FCSTD DOCUMENT  (FreeCAD 2024.2R38021 (Git))
Label: Profile__2020-V-Slot
License: All rights reserved
LicenseURL: https://en.wikipedia.org/wiki/All_rights_reserved
objects: Sketcher::SketchObject×1, PartDesign::Body×1
note: 2 computed .brp shape members not serialized (recipe doc carries the construction recipe); baked Part::Feature solids carry a one-line shape summary decoded from their .brp

FEATURE [Sketcher::SketchObject] Sketch
  AttachmentSupport = -> [YZ_Plane]
  FullyConstrained = true
  MapMode = 5
  Placement = pos=(0,0,0) rot=(0.57735,0.57735,0.57735;2.0944rad)
  sketch-geometry (61):
    g0: LineSegment StartX=-5.5 StartY=10 StartZ=0 EndX=-3.7 EndY=8.2 EndZ=0
    g1: LineSegment StartX=-3.7 StartY=8.2 StartZ=0 EndX=-5.5 EndY=8.2 EndZ=0
    g2: LineSegment StartX=-5.5 StartY=8.2 StartZ=0 EndX=-5.5 EndY=6.561 EndZ=0
    g3: LineSegment StartX=-5.5 StartY=6.561 StartZ=0 EndX=-2.639 EndY=3.7 EndZ=0
    g4: LineSegment StartX=-2.639 StartY=3.7 StartZ=0 EndX=-0.4 EndY=3.7 EndZ=0
    g5: LineSegment StartX=-10 StartY=5.5 StartZ=0 EndX=-8.2 EndY=3.7 EndZ=0
    g6: LineSegment StartX=-8.2 StartY=5.5 StartZ=0 EndX=-6.561 EndY=5.5 EndZ=0
    g7: LineSegment StartX=-6.561 StartY=5.5 StartZ=0 EndX=-3.7 EndY=2.639 EndZ=0
    g8: LineSegment StartX=-3.7 StartY=2.639 StartZ=0 EndX=-3.7 EndY=0.4 EndZ=0
    g9: LineSegment StartX=-10 StartY=5.5 StartZ=0 EndX=-10 EndY=10 EndZ=0
    g10: LineSegment StartX=-5.5 StartY=10 StartZ=0 EndX=-10 EndY=10 EndZ=0
    g11: LineSegment StartX=-10 StartY=10 StartZ=0 EndX=-1 EndY=1 EndZ=0
    g12: LineSegment StartX=-8.2 StartY=3.7 StartZ=0 EndX=-8.2 EndY=5.5 EndZ=0
    g13: LineSegment StartX=5.5 StartY=10 StartZ=0 EndX=3.7 EndY=8.2 EndZ=0
    g14: LineSegment StartX=3.7 StartY=8.2 StartZ=0 EndX=5.5 EndY=8.2 EndZ=0
    g15: LineSegment StartX=5.5 StartY=8.2 StartZ=0 EndX=5.5 EndY=6.561 EndZ=0
    g16: LineSegment StartX=5.5 StartY=6.561 StartZ=0 EndX=2.639 EndY=3.7 EndZ=0
    g17: LineSegment StartX=2.639 StartY=3.7 StartZ=0 EndX=0.4 EndY=3.7 EndZ=0
    g18: LineSegment StartX=10 StartY=5.5 StartZ=0 EndX=8.2 EndY=3.7 EndZ=0
    g19: LineSegment StartX=8.2 StartY=5.5 StartZ=0 EndX=6.561 EndY=5.5 EndZ=0
    g20: LineSegment StartX=6.561 StartY=5.5 StartZ=0 EndX=3.7 EndY=2.639 EndZ=0
    g21: LineSegment StartX=3.7 StartY=2.639 StartZ=0 EndX=3.7 EndY=0.4 EndZ=0
    g22: LineSegment StartX=10 StartY=5.5 StartZ=0 EndX=10 EndY=10 EndZ=0
    g23: LineSegment StartX=5.5 StartY=10 StartZ=0 EndX=10 EndY=10 EndZ=0
    g24: LineSegment StartX=10 StartY=10 StartZ=0 EndX=1 EndY=1 EndZ=0
    g25: LineSegment StartX=8.2 StartY=3.7 StartZ=0 EndX=8.2 EndY=5.5 EndZ=0
    g26: LineSegment StartX=-5.5 StartY=-10 StartZ=0 EndX=-3.7 EndY=-8.2 EndZ=0
    g27: LineSegment StartX=-3.7 StartY=-8.2 StartZ=0 EndX=-5.5 EndY=-8.2 EndZ=0
    g28: LineSegment StartX=-5.5 StartY=-8.2 StartZ=0 EndX=-5.5 EndY=-6.561 EndZ=0
    g29: LineSegment StartX=-5.5 StartY=-6.561 StartZ=0 EndX=-2.639 EndY=-3.7 EndZ=0
    g30: LineSegment StartX=-2.639 StartY=-3.7 StartZ=0 EndX=-0.4 EndY=-3.7 EndZ=0
    g31: LineSegment StartX=-10 StartY=-5.5 StartZ=0 EndX=-8.2 EndY=-3.7 EndZ=0
    g32: LineSegment StartX=-8.2 StartY=-5.5 StartZ=0 EndX=-6.561 EndY=-5.5 EndZ=0
    g33: LineSegment StartX=-6.561 StartY=-5.5 StartZ=0 EndX=-3.7 EndY=-2.639 EndZ=0
    g34: LineSegment StartX=-3.7 StartY=-2.639 StartZ=0 EndX=-3.7 EndY=-0.4 EndZ=0
    g35: LineSegment StartX=-10 StartY=-5.5 StartZ=0 EndX=-10 EndY=-10 EndZ=0
    g36: LineSegment StartX=-5.5 StartY=-10 StartZ=0 EndX=-10 EndY=-10 EndZ=0
    g37: LineSegment StartX=-10 StartY=-10 StartZ=0 EndX=-1 EndY=-1 EndZ=0
    g38: LineSegment StartX=-8.2 StartY=-3.7 StartZ=0 EndX=-8.2 EndY=-5.5 EndZ=0
    g39: LineSegment StartX=5.5 StartY=-10 StartZ=0 EndX=3.7 EndY=-8.2 EndZ=0
    g40: LineSegment StartX=3.7 StartY=-8.2 StartZ=0 EndX=5.5 EndY=-8.2 EndZ=0
    g41: LineSegment StartX=5.5 StartY=-8.2 StartZ=0 EndX=5.5 EndY=-6.561 EndZ=0
    g42: LineSegment StartX=5.5 StartY=-6.561 StartZ=0 EndX=2.639 EndY=-3.7 EndZ=0
    g43: LineSegment StartX=2.639 StartY=-3.7 StartZ=0 EndX=0.4 EndY=-3.7 EndZ=0
    g44: LineSegment StartX=10 StartY=-5.5 StartZ=0 EndX=8.2 EndY=-3.7 EndZ=0
    g45: LineSegment StartX=8.2 StartY=-5.5 StartZ=0 EndX=6.561 EndY=-5.5 EndZ=0
    g46: LineSegment StartX=6.561 StartY=-5.5 StartZ=0 EndX=3.7 EndY=-2.639 EndZ=0
    g47: LineSegment StartX=3.7 StartY=-2.639 StartZ=0 EndX=3.7 EndY=-0.4 EndZ=0
    g48: LineSegment StartX=10 StartY=-5.5 StartZ=0 EndX=10 EndY=-10 EndZ=0
    g49: LineSegment StartX=5.5 StartY=-10 StartZ=0 EndX=10 EndY=-10 EndZ=0
    g50: LineSegment StartX=10 StartY=-10 StartZ=0 EndX=1 EndY=-1 EndZ=0
    g51: LineSegment StartX=8.2 StartY=-3.7 StartZ=0 EndX=8.2 EndY=-5.5 EndZ=0
    g52: LineSegment StartX=-0.4 StartY=3.7 StartZ=0 EndX=0 EndY=3.3 EndZ=0
    g53: LineSegment StartX=0 StartY=3.3 StartZ=0 EndX=0.4 EndY=3.7 EndZ=0
    g54: LineSegment StartX=-0.4 StartY=-3.7 StartZ=0 EndX=1e-16 EndY=-3.3 EndZ=0
    g55: LineSegment StartX=1e-16 StartY=-3.3 StartZ=0 EndX=0.4 EndY=-3.7 EndZ=0
    g56: LineSegment StartX=-3.7 StartY=0.4 StartZ=0 EndX=-3.3 EndY=0 EndZ=0
    g57: LineSegment StartX=-3.7 StartY=-0.4 StartZ=0 EndX=-3.3 EndY=0 EndZ=0
    g58: LineSegment StartX=3.7 StartY=-0.4 StartZ=0 EndX=3.3 EndY=1e-16 EndZ=0
    g59: LineSegment StartX=3.7 StartY=0.4 StartZ=0 EndX=3.3 EndY=1e-16 EndZ=0
    g60: Circle CenterX=0 CenterY=0 CenterZ=0 NormalX=0 NormalY=0 NormalZ=1 AngleXU=0 Radius=2.1
  constraints (134):
    c: Coincident(g1,g2)
    c: Coincident(g3,g4)
    c: Coincident(g6,g7)
    c: Coincident(g7,g8)
    c: Vertical(g8)
    c: DistanceY(g-1,g5) = 5.5
    c: DistanceX(g5,g5) = 1.8
    c: Distance(g8,g-1) = 0.4
    c: DistanceY(g-1,g9) = 10
    c: DistanceX(g9,g-1) = 10
    c: Coincident(g9,g5)
    c: Vertical(g9)
    c: Coincident(g10,g0)
    c: Angle(g5,g9) = 2.35619
    c: Coincident(g11,g9)
    c: Distance(g6,g-1) = 5.5
    c: Horizontal(g6)
    c: Coincident(g12,g5)
    c: Coincident(g12,g6)
    c: Vertical(g12)
    c: DistanceY(g8,g8) = 2.239
    c: Symmetric(g5,g0,g11)
    c: Symmetric(g6,g1,g11)
    c: Symmetric(g6,g2,g11)
    c: Symmetric(g7,g3,g11)
    c: Symmetric(g8,g4,g11)
    c: Symmetric(g5,g1,g11)
    c: Coincident(g0,g1)
    c: Coincident(g9,g10)
    c: Coincident(g3,g2)
    c: DistanceX(g6,g6) = 1.639
    c: Angle(g11) = -0.785398
    c: Distance(g11,g-2) = 1
    c: DistanceX(g8,g-1) = 3.7
    c: Symmetric(g0,g13,g-2)
    c: Symmetric(g0,g13,g-2)
    c: Symmetric(g1,g14,g-2)
    c: Symmetric(g1,g14,g-2)
    c: Symmetric(g2,g15,g-2)
    c: Symmetric(g2,g15,g-2)
    c: Symmetric(g3,g16,g-2)
    c: Symmetric(g3,g16,g-2)
    c: Symmetric(g4,g17,g-2)
    c: Symmetric(g4,g17,g-2)
    c: Symmetric(g5,g18,g-2)
    c: Symmetric(g5,g18,g-2)
    c: Symmetric(g6,g19,g-2)
    c: Symmetric(g6,g19,g-2)
    c: Symmetric(g7,g20,g-2)
    c: Symmetric(g7,g20,g-2)
    c: Symmetric(g8,g21,g-2)
    c: Symmetric(g8,g21,g-2)
    c: Symmetric(g9,g22,g-2)
    c: Symmetric(g9,g22,g-2)
    c: Symmetric(g10,g23,g-2)
    c: Symmetric(g10,g23,g-2)
    c: Symmetric(g11,g24,g-2)
    c: Symmetric(g11,g24,g-2)
    c: Symmetric(g12,g25,g-2)
    c: Symmetric(g12,g25,g-2)
    c: Symmetric(g0,g26,g-1)
    c: Symmetric(g0,g26,g-1)
    c: Symmetric(g1,g27,g-1)
    c: Symmetric(g1,g27,g-1)
    c: Symmetric(g2,g28,g-1)
    c: Symmetric(g2,g28,g-1)
    c: Symmetric(g3,g29,g-1)
    c: Symmetric(g3,g29,g-1)
    c: Symmetric(g4,g30,g-1)
    c: Symmetric(g4,g30,g-1)
    c: Symmetric(g5,g31,g-1)
    c: Symmetric(g5,g31,g-1)
    c: Symmetric(g6,g32,g-1)
    c: Symmetric(g6,g32,g-1)
    c: Symmetric(g7,g33,g-1)
    c: Symmetric(g7,g33,g-1)
    c: Symmetric(g8,g34,g-1)
    c: Symmetric(g8,g34,g-1)
    c: Symmetric(g9,g35,g-1)
    c: Symmetric(g9,g35,g-1)
    c: Symmetric(g10,g36,g-1)
    c: Symmetric(g10,g36,g-1)
    c: Symmetric(g11,g37,g-1)
    c: Symmetric(g11,g37,g-1)
    c: Symmetric(g12,g38,g-1)
    c: Symmetric(g12,g38,g-1)
    c: Symmetric(g13,g39,g-1)
    c: Symmetric(g13,g39,g-1)
    c: Symmetric(g14,g40,g-1)
    c: Symmetric(g14,g40,g-1)
    c: Symmetric(g15,g41,g-1)
    c: Symmetric(g15,g41,g-1)
    c: Symmetric(g16,g42,g-1)
    c: Symmetric(g16,g42,g-1)
    c: Symmetric(g17,g43,g-1)
    c: Symmetric(g17,g43,g-1)
    c: Symmetric(g18,g44,g-1)
    c: Symmetric(g18,g44,g-1)
    c: Symmetric(g19,g45,g-1)
    c: Symmetric(g19,g45,g-1)
    c: Symmetric(g20,g46,g-1)
    c: Symmetric(g20,g46,g-1)
    c: Symmetric(g21,g47,g-1)
    c: Symmetric(g21,g47,g-1)
    c: Symmetric(g22,g48,g-1)
    c: Symmetric(g22,g48,g-1)
    c: Symmetric(g23,g49,g-1)
    c: Symmetric(g23,g49,g-1)
    c: Symmetric(g24,g50,g-1)
    c: Symmetric(g24,g50,g-1)
    c: Symmetric(g25,g51,g-1)
    c: Symmetric(g25,g51,g-1)
    c: Angle(g-1,g52) = -0.785398
    c: Coincident(g52,g4)
    c: PointOnObject(g52,g-2)
    c: Coincident(g53,g52)
    c: Coincident(g53,g17)
    c: Angle(g-1,g54) = 0.785398
    c: Coincident(g54,g30)
    c: PointOnObject(g54,g-2)
    c: Coincident(g55,g54)
    c: Coincident(g55,g43)
    c: Angle(g-1,g56) = -0.785398
    c: Coincident(g56,g8)
    c: PointOnObject(g56,g-1)
    c: Coincident(g57,g34)
    c: Coincident(g57,g56)
    c: Angle(g-1,g58) = 2.35619
    c: Coincident(g58,g47)
    c: PointOnObject(g58,g-1)
    c: Coincident(g59,g21)
    c: Coincident(g59,g58)
    c: Diameter(g60) = 4.2
    c: Coincident(g60,g-1)
FEATURE [PartDesign::Body] Body
  AllowCompound = false
  Group = -> [Sketch]
  Origin = -> Origin
